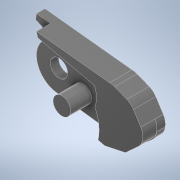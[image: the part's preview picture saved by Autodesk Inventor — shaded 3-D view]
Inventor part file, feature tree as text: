
AUTODESK INVENTOR PART (.ipt)
format: ipt  version: 2022 (Build 260153000, 153)  size: 372,224 bytes
history: native  units: in
note: dims shown in document units (in); Inventor stores cm internally (conversion verified against a paired STEP export)
features: extrude x3, sketch x2, other x1
ambient origin geometry x8: Origin, YZ Plane, XZ Plane, XY Plane, X Axis, Y Axis, Z Axis, Center Point
bodies: Body1 (feature_tree)
feature tree (6):
  other  "Sólido1"
  extrude  "Extrusión1"  Depth=0.252in
  extrude  "Extrusión5"  Depth=0.1181in
  extrude  "Extrusión6"  Depth=0.1181in
  sketch  "Boceto5"  dims[d0=0.0984in d4=0.252in]
  sketch  "Boceto6"  dims[d5=0.1634in d6=0.4055in d7=0.1496in d8=0.0709in d9=0.4331in d10=0.2756in d11=0.0472in d12=0.0in d19=0.0787in d24=0.0787in d25=0.0in d26=0.0984in d27=0.1181in d28=0.0in]
